# Revit family: R-MTD-284
name_source: partatom
category: Portes
units: mm (PartAtom-declared; Revit-internal decimal feet)

## family parameters
Couper avec des vides une fois chargée = Non
Hôte = Mur
Partagée = Non
Point de calcul de pièce = Non
Toujours verticalement = Oui

## types (1)
- MTD-284
    1 Vantail = Non
    2 Vantaux = Oui
    Angle Rail 1 = 1.00°
    Angle Rail 2 = 1.00°
    Butée en L = Non
    Butée en U = Non
    Certification = D.A.S. Mode 2 certifié NF
    Construction analytique = <Aucun>
    DAS = Oui
    DC Fixation_Rail = 150 mm  [stored 0.492126 ft]
    DC Jeu Avant = 0 mm  [stored 0 ft]
    DC Jeu Haut = 0 mm  [stored 0 ft]
    DC Portillon = 0 mm  [stored 0 ft]
    DC Profil Butée = 0 mm  [stored 0 ft]
    Description = Bloc-porte métal industriel D.A.S. M 1202 S - DAS système coulissant à rencontre composés de 2 modules coulissants de 1 panneau en hauteur, EI120, D.A.S. certifié NF, sur rail incliné ou droit, avec guidage au sol, pour baie maxi 6890x3000
    Désax 2V Asymétrique = 0 mm  [stored 0 ft]
    Ep Butée = 178 mm  [stored 0.58399 ft]
    Ep Chicane Murale = 200 mm  [stored 0.656168 ft]
    Ep Face Coté Baie = 10 mm  [stored 0.0328084 ft]
    Ep Face Coté Opposé Baie = 10 mm  [stored 0.0328084 ft]
    Ep Fond Butée = 11 mm  [stored 0.0360892 ft]
    Ep Rail = 3 mm  [stored 0.00984252 ft]
    Ep Vantail = 100 mm  [stored 0.328084 ft]
    Fabricant = MALERBA
    Fiche_Produit = MTD-284
    Fixation Linteau = Oui
    Fixation sous Dalle = Non
    Grille Vantail Principal = Non
    Grille Vantail Secondaire = Non
    Grille toute hauteur = Non
    Hauteur Baie = 2200 mm
    Hauteur Profil Rail = 44 mm
    Hauteur chandelle support grille = 180 mm  [stored 0.590551 ft]
    Hauteur sous Dalle = 2500 mm  [stored 8.2021 ft]
    Ht Fixation Linteau = 430 mm
    Ht Portillon = 2000 mm  [stored 6.56168 ft]
    Jeu Portillon Bas = 51 mm
    Jeu Portillon Coté Opposé Pivot = 10 mm  [stored 0.0328084 ft]
    Jeu Portillon Coté Pivot = 10 mm  [stored 0.0328084 ft]
    Jeu Portillon Haut = 10 mm  [stored 0.0328084 ft]
    Jeu Vantail Bas = 10 mm  [stored 0.0328084 ft]
    Larg Portillon = 900 mm  [stored 2.95276 ft]
    Larg Vantail Primaire Asymétrique = 2400 mm
    Largeur Baie = 2600 mm  [stored 8.53018 ft]
    Lgt Fix Vantail Primaire = 2650 mm
    Lgt Fix Vantail Second = 2650 mm
    Lgt Rail Second = 3150 mm  [stored 10.3346 ft]
    Mat Ame = Prépeint
    Mat Grille = Grille
    Mat Quinc = Acier galvanisé
    Mat Support = Peinture Laquée PMT - Gris Anthracite - RAL 7016
    Materiaux_Dominant = Métal
    Montage sur Mur Perpendiculaire = Non
    Note d'identification = 2V EI120 - DAS COULISSANT A RENCONTRE - 1 PANNEAU
    Position Vantail Mur = 91 mm  [stored 0.298556 ft]
    Prof Butée = 260 mm  [stored 0.853018 ft]
    Prof Chicane Murale = 50 mm  [stored 0.164042 ft]
    Prof Coté Butée = 71 mm
    Profondeur Rail = 49 mm  [stored 0.160761 ft]
    Rec Arrière = 215 mm
    Rec Avant = 160 mm  [stored 0.524934 ft]
    Rec Haut = 200 mm  [stored 0.656168 ft]
    Reference_Commerciale = M 1202 S - DAS
    Resistance_Feu = EI120
    Retours Rails = 17 mm
    Sens_Feu = Recto/ Verso
    Thermique (W/m2.°K) = 0
    URL = https://www.malerba.fr
    Vantaux Asymétriques = Non
    lgt Rail Primaire = 3150 mm  [stored 10.3346 ft]

note: [stored X ft] marks values corroborated as IEEE doubles in the binary element streams (Revit-internal decimal feet)

## geometry (parser evidence)
native form markers: Blend x12
no freeform markers — native parametric forms only
